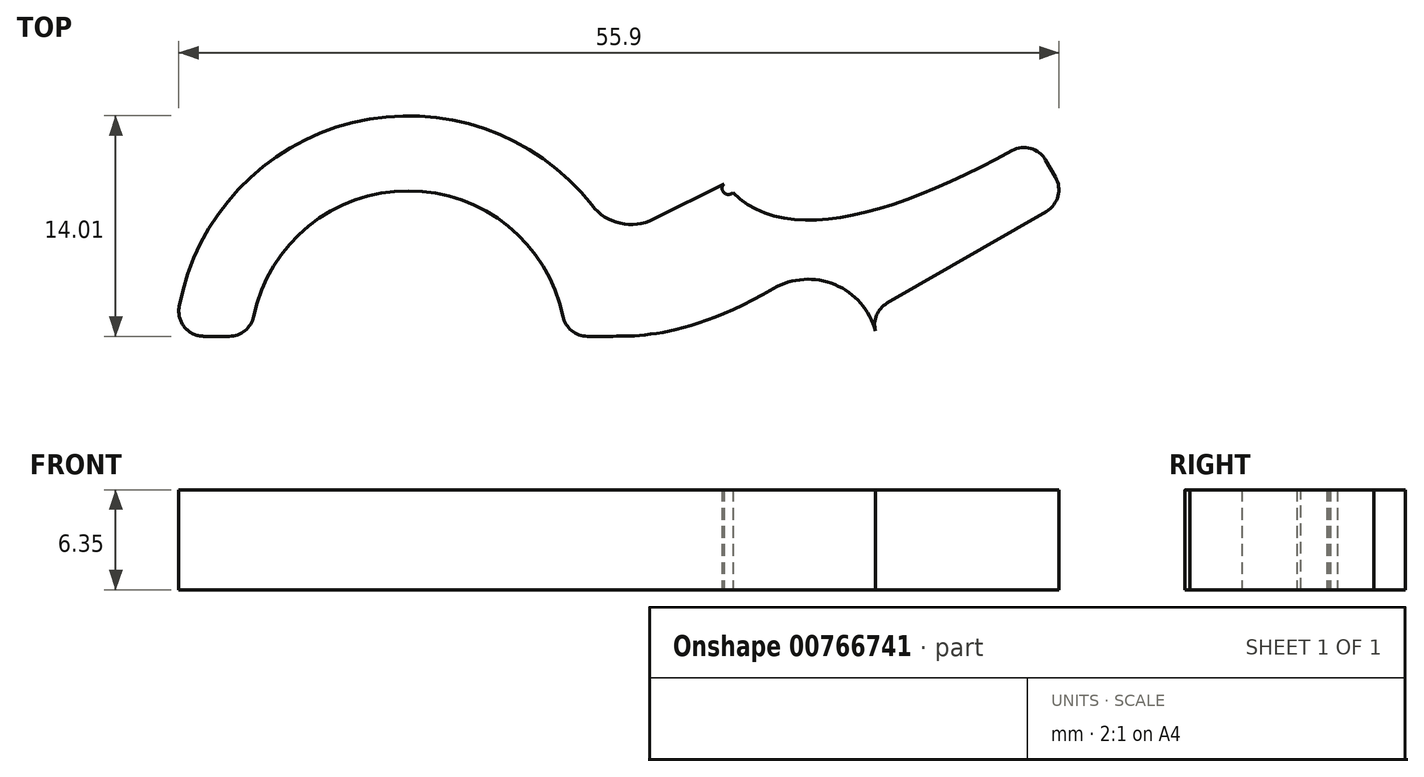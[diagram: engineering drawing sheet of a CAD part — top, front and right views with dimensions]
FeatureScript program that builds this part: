
annotation { "Feature Type Name" : "Feature", "Feature Type Description" : "" }
export const myFeature = defineFeature(function(context is Context, id is Id, definition is map)
    precondition{}
    {
        {
            var Q0;
            Q0=qCreatedBy(makeId("Top.planeOp"),FACE);
            var sketch = newSketch(context, id + "F0", { "sketchPlane" : qUnion([Q0])});
            skCircle(sketch, "E0", {"center": v(0, 0) * mm, "radius": 3.62 * mm, "construction": true});
            skLineSegment(sketch, "E1", {"start": v(2.56, 2.56) * mm, "end": v(-5.07, 10.2) * mm, "construction": true});
            skLineSegment(sketch, "E2", {"start": v(2.56, -2.56) * mm, "end": v(-5.07, -10.2) * mm, "construction": true});
            skCircle(sketch, "E3", {"center": v(-25.4, 0) * mm, "radius": 4.95 * mm, "construction": true});
            skCircle(sketch, "E4.0", {"center": v(-25.4, 0) * mm, "radius": 11.3 * mm, "construction": true});
            skLineSegment(sketch, "E5", {"start": v(0, 0) * mm, "end": v(-35.43, 0) * mm});
            skArc(sketch, "E6", {"start": v(-39.95, -2.67) * mm, "mid": v(-25.4, -14.8) * mm, "end": v(-10.85, -2.67) * mm});
            skArc(sketch, "E7", {"start": v(-13.75, 9.12) * mm, "mid": v(-28.93, 14.37) * mm, "end": v(-39.95, 2.67) * mm});
            skLineSegment(sketch, "E8", {"start": v(-35.43, 0) * mm, "end": v(-40.2, 0) * mm});
            skArc(sketch, "E9", {"start": v(-35.22, -2.06) * mm, "mid": v(-25.4, -10.03) * mm, "end": v(-15.58, -2.06) * mm});
            skArc(sketch, "E10", {"start": v(-15.58, 2.06) * mm, "mid": v(-25.4, 10.03) * mm, "end": v(-35.22, 2.06) * mm});
            skLineSegment(sketch, "E11", {"start": v(-38.4, 0.8) * mm, "end": v(-36.77, 0.8) * mm});
            skLineSegment(sketch, "E12", {"start": v(-36.77, -0.8) * mm, "end": v(-38.4, -0.8) * mm});
            skPoint(sketch, "E13.newPointB", {"position": v(-51.13, 0.8) * mm});
            skArc(sketch, "E13.filletArc", {"start": v(-39.95, 2.67) * mm, "mid": v(-39.61, 1.36) * mm, "end": v(-38.4, 0.8) * mm});
            skArc(sketch, "E14.filletArc", {"start": v(-36.77, 0.8) * mm, "mid": v(-35.77, 1.15) * mm, "end": v(-35.22, 2.06) * mm});
            skPoint(sketch, "E15.newPointB", {"position": v(-51.13, -0.8) * mm});
            skArc(sketch, "E15.filletArc", {"start": v(-38.4, -0.8) * mm, "mid": v(-39.61, -1.36) * mm, "end": v(-39.95, -2.67) * mm});
            skPoint(sketch, "E16.newPointA", {"position": v(-11.12, -0.8) * mm});
            skArc(sketch, "E16.filletArc", {"start": v(-35.22, -2.06) * mm, "mid": v(-35.77, -1.15) * mm, "end": v(-36.77, -0.8) * mm});
            skArc(sketch, "E17.0", {"start": v(4.41, 0) * mm, "mid": v(2.2, 3.82) * mm, "end": v(-2.2, 3.82) * mm});
            skCircle(sketch, "E18", {"center": v(-5.07, 10.2) * mm, "radius": 0.4 * mm});
            skCircle(sketch, "E19", {"center": v(-5.07, -10.2) * mm, "radius": 0.4 * mm});
            skLineSegment(sketch, "E20", {"start": v(-14.03, 0.8) * mm, "end": v(-12.4, 0.8) * mm});
            skLineSegment(sketch, "E21", {"start": v(-12.4, -0.8) * mm, "end": v(-14.03, -0.8) * mm});
            skPoint(sketch, "E22.visualSharp", {"position": v(-15.4, 0.8) * mm});
            skArc(sketch, "E22.filletArc", {"start": v(-15.58, 2.06) * mm, "mid": v(-15.03, 1.15) * mm, "end": v(-14.03, 0.8) * mm});
            skPoint(sketch, "E23.visualSharp", {"position": v(-10.63, 0.8) * mm});
            skPoint(sketch, "E24.visualSharp", {"position": v(-10.63, -0.8) * mm});
            skArc(sketch, "E24.filletArc", {"start": v(-10.85, -2.67) * mm, "mid": v(-11.19, -1.36) * mm, "end": v(-12.4, -0.8) * mm});
            skPoint(sketch, "E25.visualSharp", {"position": v(-15.4, -0.8) * mm});
            skArc(sketch, "E25.filletArc", {"start": v(-14.03, -0.8) * mm, "mid": v(-15.03, -1.15) * mm, "end": v(-15.58, -2.06) * mm});
            skLineSegment(sketch, "E26", {"start": v(-2.2, 3.82) * mm, "end": v(14.3, 13.35) * mm, "construction": true});
            skLineSegment(sketch, "E27", {"start": v(-5.07, 10.2) * mm, "end": v(-25.4, 0) * mm, "construction": true});
            skLineSegment(sketch, "E28", {"start": v(-5.07, -10.2) * mm, "end": v(-25.4, 0) * mm, "construction": true});
            skLineSegment(sketch, "E29", {"start": v(-9.82, 8.23) * mm, "end": v(-5.35, 10.47) * mm});
            skLineSegment(sketch, "E30", {"start": v(-12.17, -6.63) * mm, "end": v(-5.27, -10.54) * mm});
            skLineSegment(sketch, "E31", {"start": v(-5.07, 10.2) * mm, "end": v(-5.35, 9.91) * mm, "construction": true});
            skLineSegment(sketch, "E32", {"start": v(-5.07, 10.2) * mm, "end": v(-5.35, 10.47) * mm, "construction": true});
            skPoint(sketch, "E33", {"position": v(-4.8, 9.91) * mm});
            skFitSpline(sketch, "E34", {"points": [v(-4.8, 9.91) * mm, v(14.3, 13.35) * mm], "startDerivative": vector(10.6, -10.6) * mm, "endDerivative": vector(24.75, 14.29) * mm});
            skLineSegment(sketch, "E35", {"start": v(15.08, 11.99) * mm, "end": v(15.7, 10.9) * mm});
            skArc(sketch, "E36.filletArc", {"start": v(-13.75, 9.12) * mm, "mid": v(-11.94, 7.97) * mm, "end": v(-9.82, 8.23) * mm});
            skArc(sketch, "E37.filletArc", {"start": v(15.08, 11.99) * mm, "mid": v(14.13, 12.72) * mm, "end": v(12.94, 12.58) * mm});
            skLineSegment(sketch, "E38", {"start": v(0, 0) * mm, "end": v(42.6, 0) * mm, "construction": true});
            skPoint(sketch, "E39", {"position": v(4.41, 0) * mm});
            skFitSpline(sketch, "E40", {"points": [v(-12.4, 0.8) * mm, v(-2.2, 3.82) * mm], "startDerivative": vector(5.35, 0) * mm, "endDerivative": vector(15.74, 9.08) * mm});
            skLineSegment(sketch, "E41", {"start": v(-7.45, 0.8) * mm, "end": v(-2.2, 3.82) * mm, "construction": true});
            skLineSegment(sketch, "E42", {"start": v(0, 0) * mm, "end": v(21.52, 12.42) * mm, "construction": true});
            skLineSegment(sketch, "E43", {"start": v(15.12, 8.73) * mm, "end": v(5.01, 2.9) * mm});
            skPoint(sketch, "E44.visualSharp", {"position": v(16.5, 9.53) * mm});
            skArc(sketch, "E44.filletArc", {"start": v(15.12, 8.73) * mm, "mid": v(15.86, 9.7) * mm, "end": v(15.7, 10.9) * mm});
            skArc(sketch, "E45", {"start": v(5.01, 2.9) * mm, "mid": v(4.34, 2.13) * mm, "end": v(4.27, 1.12) * mm});
            skSolve(sketch);
        }
        {
            var Q0;
            Q0=makeQuery(id+"F0.imprint","IMPRINT",FACE,{"disambiguationData":[TD([[makeQuery(id+"F0.imprint","IMPRINT",EDGE,{"derivedFrom":sQuery(id+"F0.wireOp",EDGE,"E7")}),1.0]])]});
            extrude(context, id + "F1", {"entities" : qUnion([Q0]), "depth" : 6.35 * mm, "offsetDistance" : 25.4 * mm});
        }
    });
